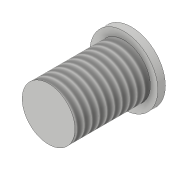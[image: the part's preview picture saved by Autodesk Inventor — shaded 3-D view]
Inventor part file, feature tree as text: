
AUTODESK INVENTOR PART (.ipt)
format: ipt  version: 2019 (Build 230136000, 136)  size: 96,768 bytes
history: native  units: in
note: dims shown in document units (in); Inventor stores cm internally (conversion verified against a paired STEP export)
features: sketch x3, extrude x2, thread x1
ambient origin geometry x8: Origin, YZ Plane, XZ Plane, XY Plane, X Axis, Y Axis, Z Axis, Center Point
bodies: Solid1 (feature_tree)
feature tree (6):
  extrude  "Extrusion1"  Depth=0.0394in TaperAngle=0.0deg
  sketch  "Sketch2"  dims[d3=0.2756in d4=0.3937in d5=0.0in d6=0.3937in d7=0.0in]
  extrude  "Extrusion2"  Depth=0.3937in TaperAngle=0.0deg
  thread  "Thread1"  [1 undecoded]
  sketch  "Sketch1"  dims[d0=0.3543in d1=0.0394in d2=0.0in]
  sketch  "Sketch3"
note: 1 required parameter value undecoded (feature->parameter linkage not recoverable at this tier; creation-order binding heuristic only, values carry confidence <= 0.55)
